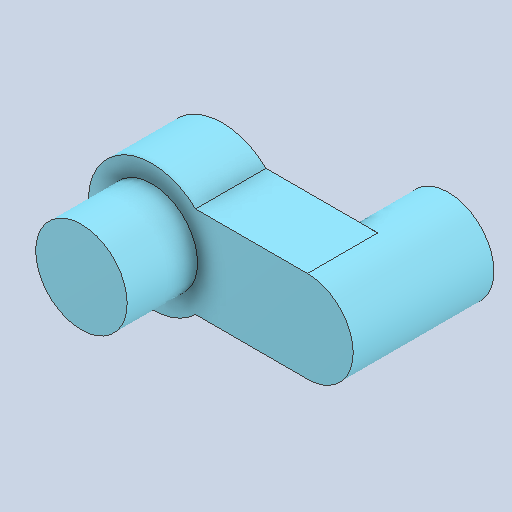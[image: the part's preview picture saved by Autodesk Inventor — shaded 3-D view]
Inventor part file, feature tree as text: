
AUTODESK INVENTOR PART (.ipt)
format: ipt  version: 2022 (Build 260153000, 153)  size: 123,392 bytes
history: native  units: in
note: dims shown in document units (in); Inventor stores cm internally (conversion verified against a paired STEP export)
features: other x3, sketch x2
ambient origin geometry x8: Origin, YZ Plane, XZ Plane, XY Plane, X Axis, Y Axis, Z Axis, Center Point
bodies: Solid1 (feature_tree)
feature tree (5):
  other  "Component31.ipt"
  other  "Solid1::Component31.ipt"
  other  "TaggingFeature1"
  sketch  "Sketch2"  dims[d0=0.3937in]
  sketch  "Sketch3"
